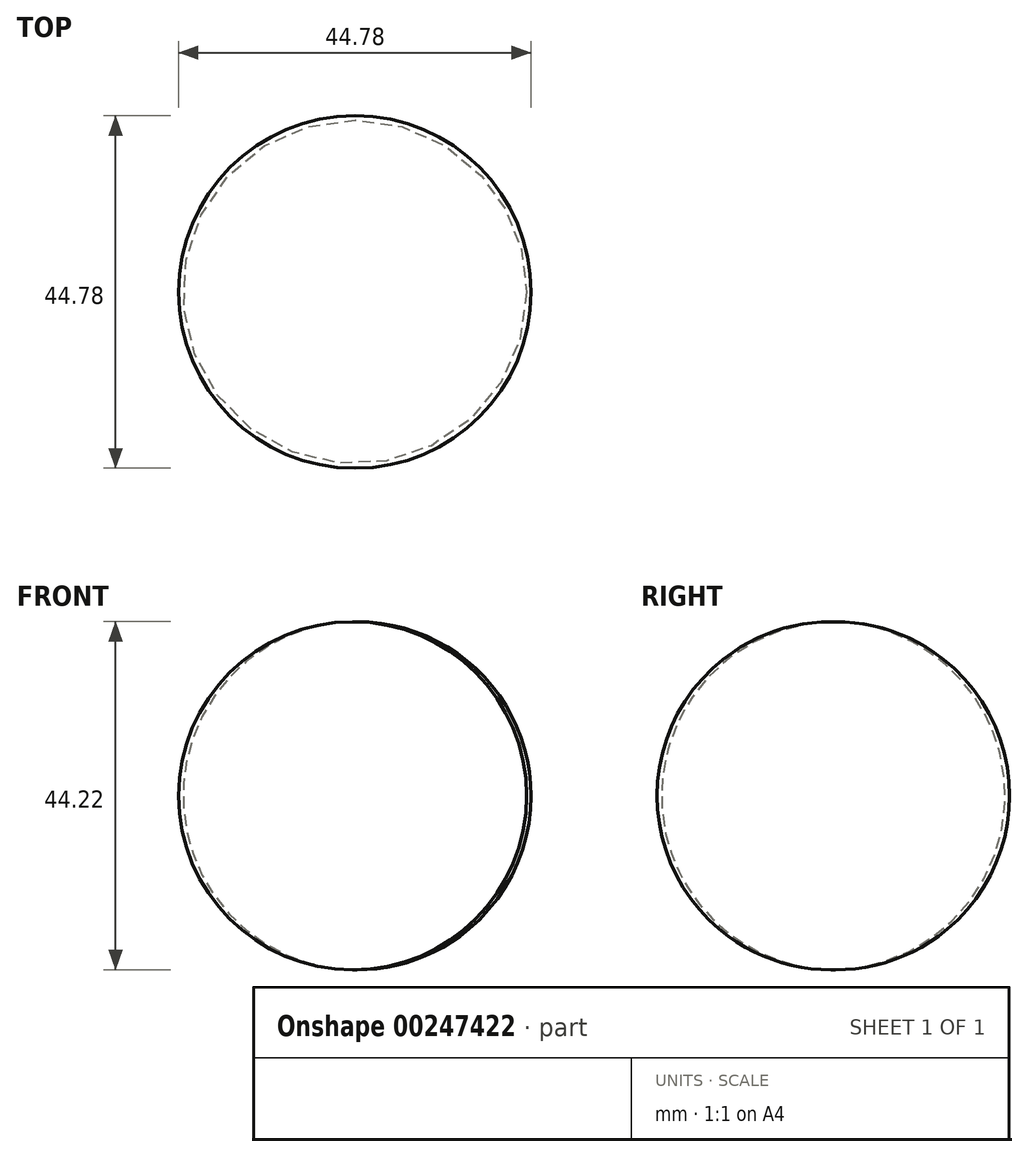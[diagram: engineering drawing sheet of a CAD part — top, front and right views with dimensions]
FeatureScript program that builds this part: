
annotation { "Feature Type Name" : "Feature", "Feature Type Description" : "" }
export const myFeature = defineFeature(function(context is Context, id is Id, definition is map)
    precondition{}
    {
        {
            var Q0;
            Q0=qCreatedBy(makeId("Front.planeOp"),FACE);
            var sketch = newSketch(context, id + "F0", { "sketchPlane" : qUnion([Q0])});
            skLineSegment(sketch, "E0", {"start": v(0, 0) * mm, "end": v(0, 44.22) * mm});
            skArc(sketch, "E1", {"start": v(0, 0) * mm, "mid": v(22.4, 22.1) * mm, "end": v(0, 44.22) * mm});
            skSolve(sketch);
        }
        {
            var Q0;
            Q0 = qSketchRegion(id + "F0", true);
            var Q1;
            Q1=sQuery(id+"F0.wireOp",EDGE,"E0");
            revolve(context, id + "F1", {"entities" : qUnion([Q0]), "axis" : qUnion([Q1]), "revolveType" : RevolveType.FULL});
        }
    });
